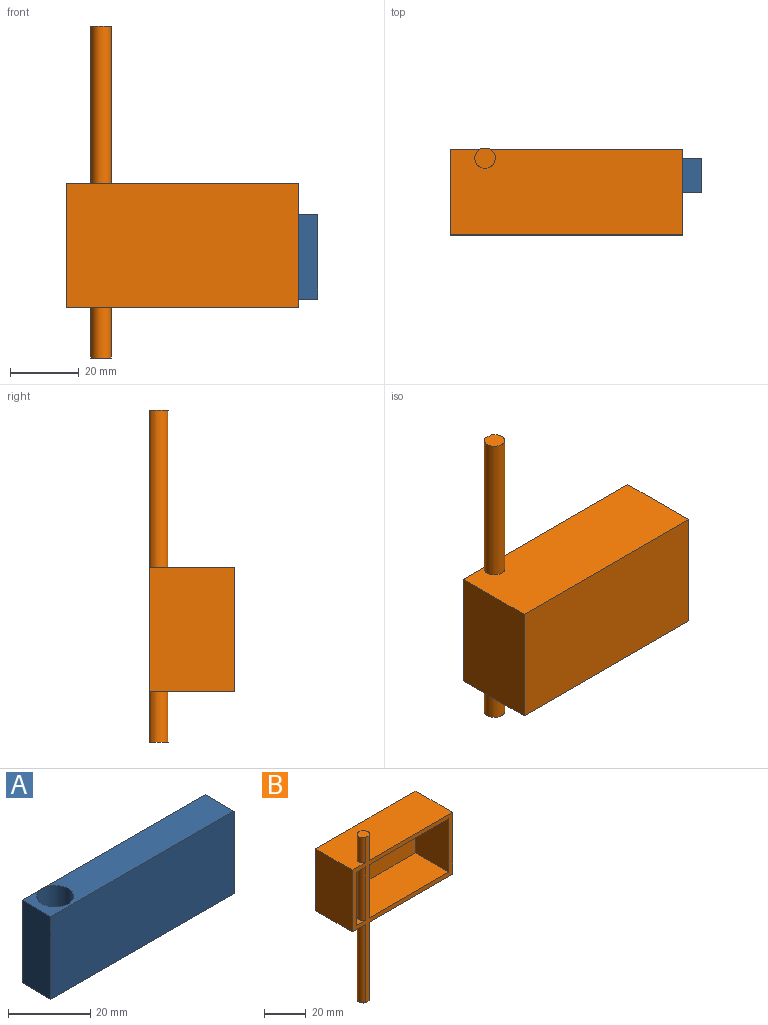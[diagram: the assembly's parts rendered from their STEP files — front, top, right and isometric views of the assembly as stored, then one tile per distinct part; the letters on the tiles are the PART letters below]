
ASSEMBLY  parts=2 mates=1
PART A: 7 faces, bbox 63.1x10x24.7 mm
  f0: plane 24.7x10mm, normal (-1,0,0), area 247mm2, adj f1,f3,f4,f5
  f1: plane 63.11x10mm, normal (0,0,-1), area 567.1mm2, adj f0,f2,f4,f5,f6
  f2: plane 24.7x10mm, normal (1,0,0), area 247mm2, adj f1,f3,f4,f5
  f3: plane 63.11x10mm, normal (0,0,1), area 567.1mm2, adj f0,f2,f4,f5,f6
  f4: plane 63.11x24.7mm, normal (0,-1,0), area 1558.5mm2, adj f0,f1,f2,f3
  f5: plane 63.11x24.7mm, normal (0,1,0), area 1558.5mm2, adj f0,f1,f2,f3
  f6: cylinder r=4.51mm len=24.7mm, axis (0,0,-1), area 700.3mm2, adj f1,f3
PART B: 16 faces, bbox 67.8x25x96.8 mm
  f0: plane 36.22x25mm, normal (-1,0,0), area 905.5mm2, adj f1,f3,f4,f5
  f1: plane 67.77x25mm, normal (0,0,-1), area 1667.1mm2, adj f0,f2,f4,f5,f14
  f2: plane 36.22x25mm, normal (1,0,0), area 905.5mm2, adj f1,f3,f4,f5
  f3: plane 67.77x25mm, normal (0,0,1), area 1667.1mm2, adj f0,f2,f4,f5,f13
  f4: plane 96.8x67.77mm, normal (0,-1,0), area 740.7mm2, adj f0,f1,f2,f3,f6,f7,f8,f9
  f5: plane 67.77x36.22mm, normal (0,1,0), area 2454.8mm2, adj f0,f1,f2,f3
  f6: plane 31.22x22.5mm, normal (1,0,0), area 702.4mm2, adj f4,f7,f9,f10
  f7: plane 62.77x22.5mm, normal (0,0,1), area 1385.2mm2, adj f4,f6,f8,f10,f11
  f8: plane 31.22x22.5mm, normal (-1,0,0), area 702.4mm2, adj f4,f7,f9,f10
  f9: plane 62.77x22.5mm, normal (0,0,-1), area 1385.2mm2, adj f4,f6,f8,f10,f11
  f10: plane 62.77x31.22mm, normal (0,-1,0), area 1959.8mm2, adj f6,f7,f8,f9
  f11: cylinder r=2.97mm len=31.22mm, axis (0,0,-1), area 496.8mm2, adj f4,f7,f9
  f12: plane 5.95x5.63mm, normal (0,0,1), area 27.2mm2, adj f4,f13
  f13: cylinder r=2.97mm len=14.68mm, axis (0,0,-1), area 233.6mm2, adj f3,f4,f12
  f14: cylinder r=2.97mm len=45.9mm, axis (0,0,-1), area 730.4mm2, adj f1,f4,f15
  f15: plane 5.95x5.63mm, normal (0,0,-1), area 27.2mm2, adj f4,f14
PLACE A t=(14.28,-27.05,-117.62)mm
PLACE B rot(axis=(1,0,0),180deg) t=(41.23,-49.39,-162.11)mm fixed
MATE revolute B.f11 <-> A.f1  axis (0,0,1) through (11.95,-27.05,-172.64)mm
